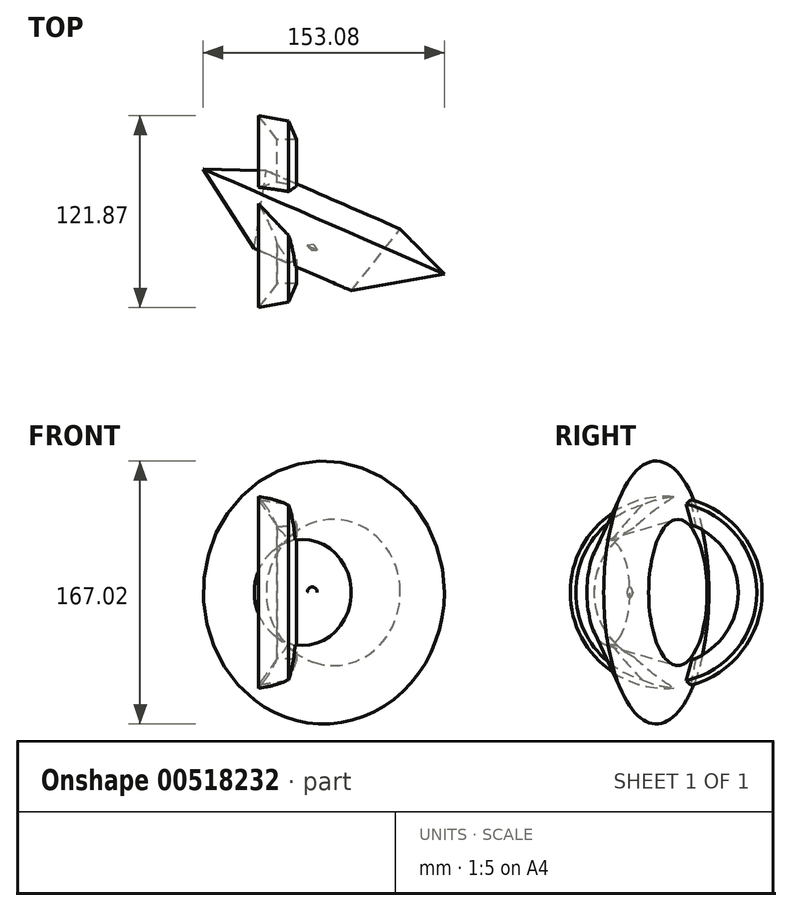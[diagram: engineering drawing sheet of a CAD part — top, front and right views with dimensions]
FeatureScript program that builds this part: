
annotation { "Feature Type Name" : "Feature", "Feature Type Description" : "" }
export const myFeature = defineFeature(function(context is Context, id is Id, definition is map)
    precondition{}
    {
        {
            var Q0;
            Q0=qCreatedBy(makeId("Top.planeOp"),FACE);
            var sketch = newSketch(context, id + "F0", { "sketchPlane" : qUnion([Q0])});
            skLineSegment(sketch, "E0", {"start": v(-18.3, 39.71) * mm, "end": v(61.7, 39.71) * mm});
            skLineSegment(sketch, "E1", {"start": v(21.7, -51.94) * mm, "end": v(61.7, 39.71) * mm});
            skLineSegment(sketch, "E2", {"start": v(-18.3, 39.71) * mm, "end": v(21.7, -51.94) * mm});
            skLineSegment(sketch, "E3", {"start": v(41.7, -6.11) * mm, "end": v(21.7, 39.71) * mm});
            skLineSegment(sketch, "E4", {"start": v(1.7, -6.11) * mm, "end": v(21.7, 39.71) * mm});
            skLineSegment(sketch, "E5", {"start": v(1.7, -6.11) * mm, "end": v(41.7, -6.11) * mm});
            skLineSegment(sketch, "E6", {"start": v(17.37, -21.22) * mm, "end": v(79.5, 57.15) * mm});
            skLineSegment(sketch, "E7", {"start": v(17.37, -21.22) * mm, "end": v(135.48, 0) * mm});
            skLineSegment(sketch, "E8", {"start": v(79.5, 57.15) * mm, "end": v(135.48, 0) * mm});
            skLineSegment(sketch, "E9", {"start": v(48.43, 17.96) * mm, "end": v(107.49, 28.57) * mm});
            skLineSegment(sketch, "E10", {"start": v(107.49, 28.57) * mm, "end": v(76.42, -10.6) * mm});
            skLineSegment(sketch, "E11", {"start": v(76.42, -10.6) * mm, "end": v(48.43, 17.96) * mm});
            skSolve(sketch);
        }
        {
            var Q0;
            Q0=makeQuery(id+"F0.imprint","IMPRINT",FACE,{"disambiguationData":[TD([[makeQuery(id+"F0.imprint","IMPRINT",EDGE,{"derivedFrom":sQuery(id+"F0.wireOp",EDGE,"E9")}),-1.0]])]});
            var Q1;
            Q1=sQuery(id+"F0.wireOp",EDGE,"E1");
            revolve(context, id + "F1", {"entities" : qUnion([Q0]), "axis" : qUnion([Q1]), "revolveType" : RevolveType.FULL});
        }
        {
            var Q0;
            {var subQ3=sQuery(id+"F0.wireOp",EDGE,"E5");Q0=makeQuery(id+"F0.imprint","IMPRINT",FACE,{"disambiguationData":[TD([[makeQuery(id+"F0.imprint","IMPRINT",EDGE,{"derivedFrom":subQ3}),-1.0]])]});}
            var Q1;
            Q1=sQuery(id+"F0.wireOp",EDGE,"E0");
            revolve(context, id + "F2", {"operationType" : NewBodyOperationType.ADD, "entities" : qUnion([Q0]), "axis" : qUnion([Q1]), "revolveType" : RevolveType.FULL});
        }
        {
            var Q0;
            {var subQ3=sQuery(id+"F0.wireOp",EDGE,"E10");Q0=makeQuery(id+"F0.imprint","IMPRINT",FACE,{"disambiguationData":[TD([[makeQuery(id+"F0.imprint","IMPRINT",EDGE,{"derivedFrom":subQ3}),1.0]])]});}
            var Q1;
            Q1=sQuery(id+"F0.wireOp",EDGE,"E1");
            revolve(context, id + "F3", {"operationType" : NewBodyOperationType.ADD, "entities" : qUnion([Q0]), "axis" : qUnion([Q1]), "revolveType" : RevolveType.FULL});
        }
    });
